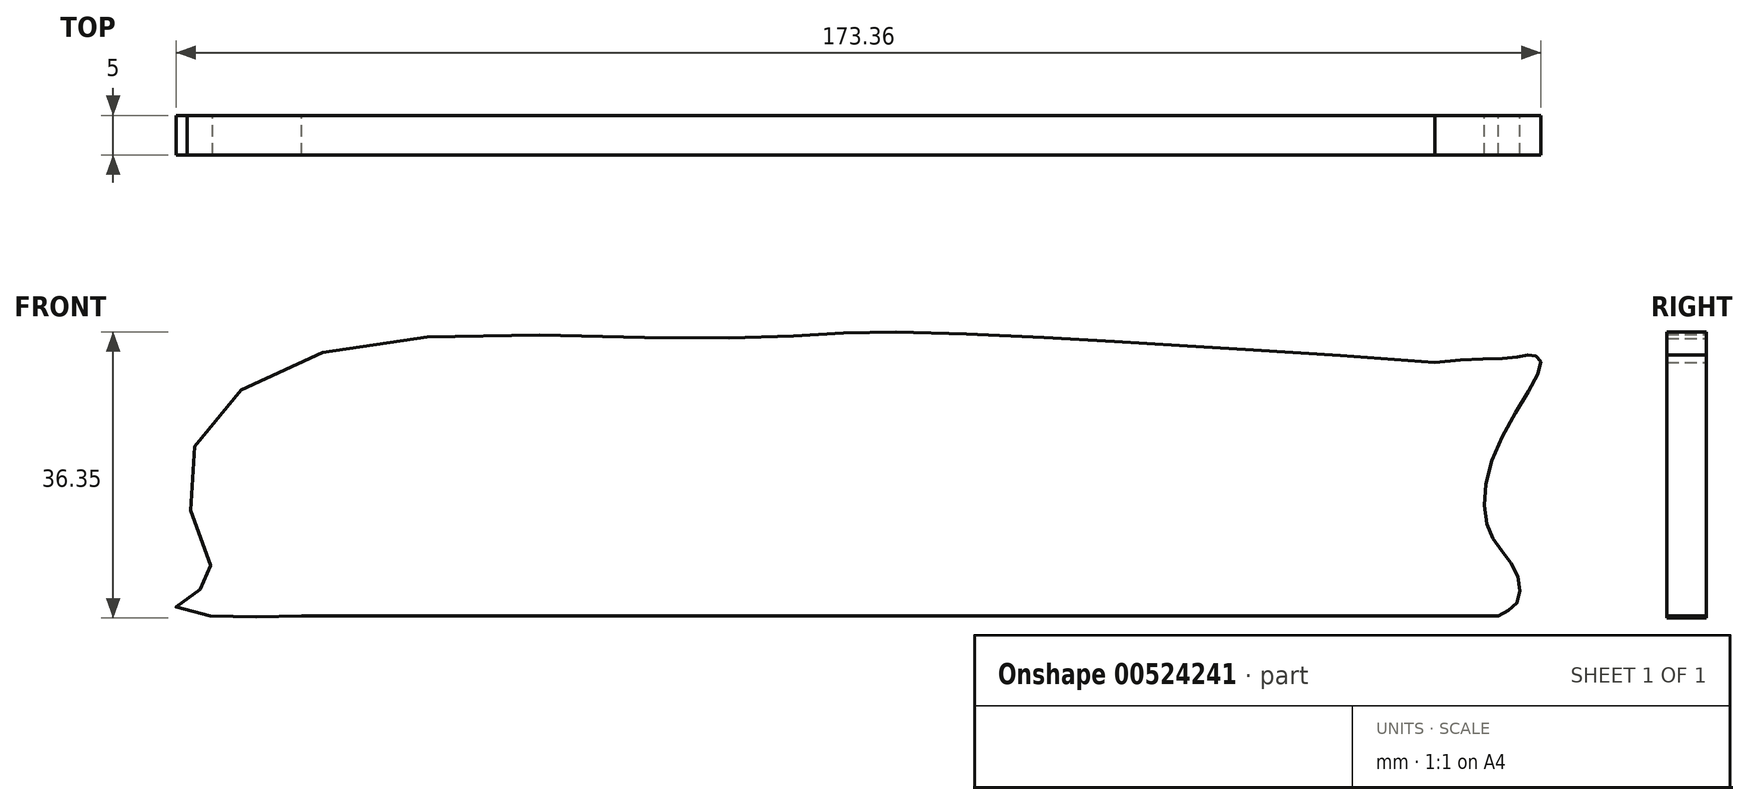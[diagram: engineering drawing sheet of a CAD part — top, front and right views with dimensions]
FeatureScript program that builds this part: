
annotation { "Feature Type Name" : "Feature", "Feature Type Description" : "" }
export const myFeature = defineFeature(function(context is Context, id is Id, definition is map)
    precondition{}
    {
        {
            var Q0;
            Q0=qCreatedBy(makeId("Front.planeOp"),FACE);
            var sketch = newSketch(context, id + "F0", { "sketchPlane" : qUnion([Q0])});
            skLineSegment(sketch, "E0", {"start": v(-70.5, -0.35) * mm, "end": v(81.54, -0.35) * mm});
            skFitSpline(sketch, "E1", {"points": [v(78.58, 31.5) * mm, v(45.66, 33.78) * mm, v(26.9, 34.86) * mm, v(4.57, 35.75) * mm, v(-5.84, 35.34) * mm, v(-27.1, 35.02) * mm, v(-72.69, 31.5) * mm, v(-85.02, 15.6) * mm, v(-81.84, 4.27) * mm, v(-84.84, 2.43) * mm, v(-86.32, 0.44) * mm, v(-77.88, -0.35) * mm, v(-70.5, -0.35) * mm], "startDerivative": vector(-288.56, 23.16) * mm, "endDerivative": vector(233.17, 27.06) * mm});
            skFitSpline(sketch, "E2", {"points": [v(81.54, -0.35) * mm, v(84.02, 1.52) * mm, v(83.4, 6.02) * mm, v(80.3, 10.63) * mm, v(81.54, 21.37) * mm, v(86.94, 31.78) * mm, v(86.09, 32.8) * mm, v(83.83, 32.55) * mm, v(73.5, 31.9) * mm], "startDerivative": vector(28.7, 15.54) * mm, "endDerivative": vector(-76, -9.77) * mm});
            skSolve(sketch);
        }
        {
            var Q0;
            {var subQ0=sQuery(id+"F0.wireOp",EDGE,"E0");Q0=makeQuery(id+"F0.imprint","IMPRINT",FACE,{"disambiguationData":[TD([[makeQuery(id+"F0.imprint","IMPRINT",EDGE,{"derivedFrom":subQ0}),1.0]])]});}
            extrude(context, id + "F1", {"entities" : qUnion([Q0]), "depth" : 5 * mm, "offsetDistance" : 25.4 * mm});
        }
    });
